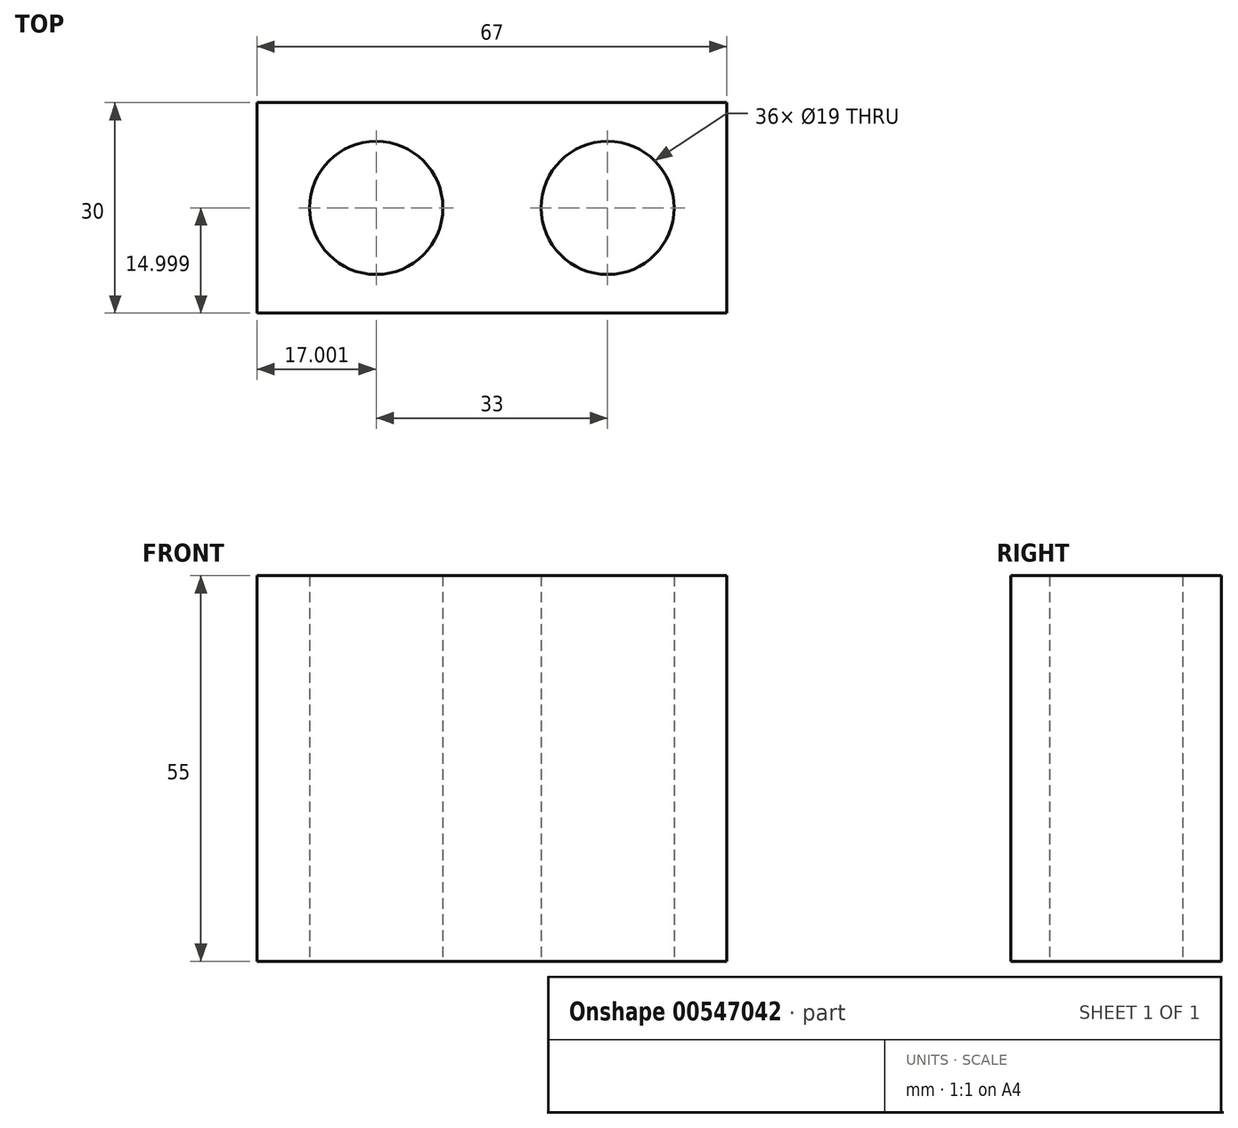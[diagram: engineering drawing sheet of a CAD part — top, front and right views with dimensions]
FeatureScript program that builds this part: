
annotation { "Feature Type Name" : "Feature", "Feature Type Description" : "" }
export const myFeature = defineFeature(function(context is Context, id is Id, definition is map)
    precondition{}
    {
        {
            var Q0;
            Q0=qCreatedBy(makeId("Top.planeOp"),FACE);
            var sketch = newSketch(context, id + "F0", { "sketchPlane" : qUnion([Q0])});
            skCircle(sketch, "E0", {"center": v(-35.84, 32.54) * mm, "radius": 9.5 * mm});
            skCircle(sketch, "E1", {"center": v(-2.84, 32.54) * mm, "radius": 9.5 * mm});
            skLineSegment(sketch, "E2.bottom", {"start": v(-52.84, 47.54) * mm, "end": v(14.16, 47.54) * mm});
            skLineSegment(sketch, "E2.top", {"start": v(-52.84, 17.54) * mm, "end": v(14.16, 17.54) * mm});
            skLineSegment(sketch, "E2.left", {"start": v(-52.84, 47.54) * mm, "end": v(-52.84, 17.54) * mm});
            skLineSegment(sketch, "E2.right", {"start": v(14.16, 47.54) * mm, "end": v(14.16, 17.54) * mm});
            skSolve(sketch);
        }
        {
            var Q0;
            Q0=makeQuery(id+"F0.imprint","IMPRINT",FACE,{"disambiguationData":[TD([[makeQuery(id+"F0.imprint","IMPRINT",EDGE,{"derivedFrom":sQuery(id+"F0.wireOp",EDGE,"E0")}),-1.0]])]});
            extrude(context, id + "F1", {"entities" : qUnion([Q0]), "depth" : 55 * mm, "offsetDistance" : 25 * mm});
        }
    });
